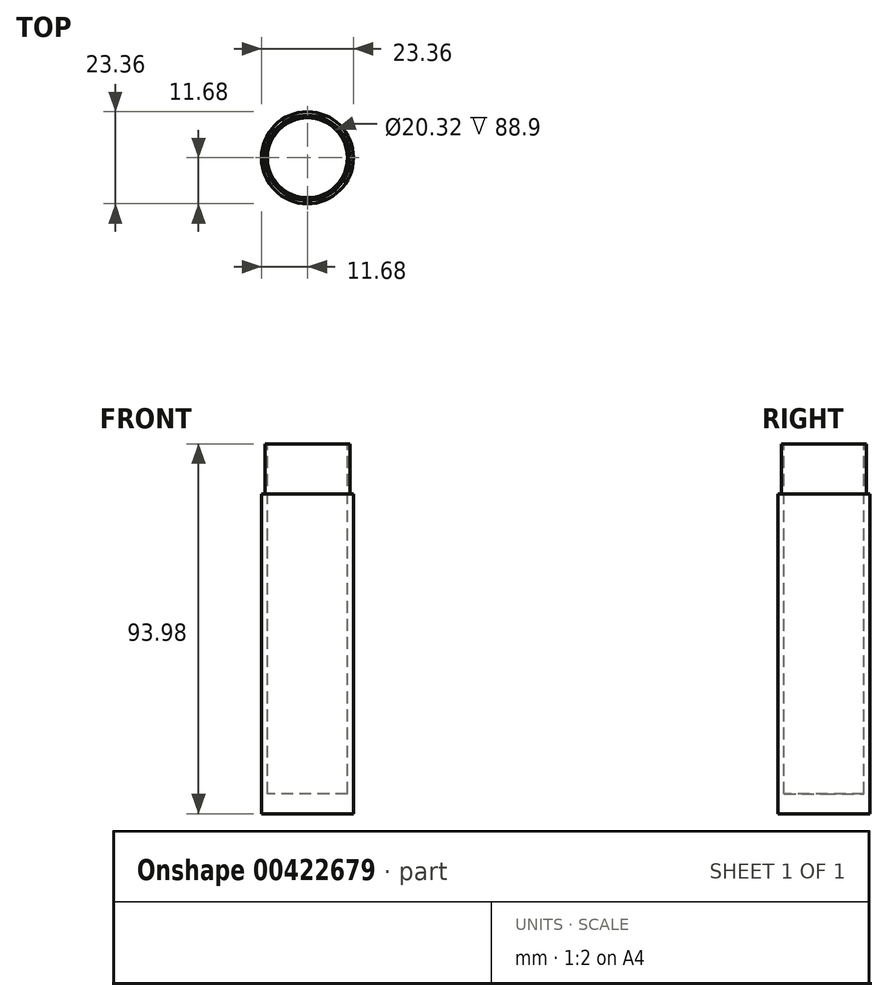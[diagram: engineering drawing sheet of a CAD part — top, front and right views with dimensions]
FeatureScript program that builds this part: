
annotation { "Feature Type Name" : "Feature", "Feature Type Description" : "" }
export const myFeature = defineFeature(function(context is Context, id is Id, definition is map)
    precondition{}
    {
        {
            var Q0;
            Q0=qCreatedBy(makeId("Top.planeOp"),FACE);
            var sketch = newSketch(context, id + "F0", { "sketchPlane" : qUnion([Q0])});
            skCircle(sketch, "E0", {"center": v(0, 0) * mm, "radius": 11.68 * mm});
            skSolve(sketch);
        }
        {
            var Q0;
            Q0=makeQuery(id+"F0.imprint","IMPRINT",FACE,{"disambiguationData":[TD([[makeQuery(id+"F0.imprint","IMPRINT",EDGE,{"derivedFrom":sQuery(id+"F0.wireOp",EDGE,"E0")}),1.0]])]});
            extrude(context, id + "F1", {"entities" : qUnion([Q0]), "depth" : 78.74 * mm});
        }
        {
            var Q0;
            Q0=makeQuery(id+"F1.opExtrude","CAP_FACE",FACE,{"disambiguationData":[OSD([sQuery(id+"F0.wireOp",EDGE,"E0")])],"isStart":false});
            var sketch = newSketch(context, id + "F2", { "sketchPlane" : qUnion([Q0])});
            skCircle(sketch, "E1", {"center": v(0, 0) * mm, "radius": 10.16 * mm});
            skSolve(sketch);
        }
        {
            var Q0;
            Q0=makeQuery(id+"F2.imprint","IMPRINT",FACE,{"disambiguationData":[TD([[makeQuery(id+"F2.imprint","IMPRINT",EDGE,{"derivedFrom":sQuery(id+"F2.wireOp",EDGE,"E1")}),1.0]])]});
            extrude(context, id + "F3", {"entities" : qUnion([Q0]), "operationType" : NewBodyOperationType.REMOVE, "oppositeDirection" : true, "depth" : 76.2 * mm});
        }
        {
            var Q0;
            Q0=makeQuery(id+"F1.opExtrude","CAP_FACE",FACE,{"disambiguationData":[OSD([sQuery(id+"F0.wireOp",EDGE,"E0")])],"isStart":true});
            extrude(context, id + "F4", {"entities" : qUnion([Q0]), "operationType" : NewBodyOperationType.ADD, "depth" : 2.54 * mm});
        }
        {
            var Q0;
            Q0=makeQuery(id+"F4.opExtrude","CAP_FACE",FACE,{"disambiguationData":[OSD([sQuery(id+"F0.wireOp",EDGE,"E0")])],"isStart":false});
            extrude(context, id + "F5", {"entities" : qUnion([Q0]), "operationType" : NewBodyOperationType.ADD, "depth" : 7.62 * mm});
        }
        {
            var Q0;
            Q0=makeQuery(id+"F2.imprint","IMPRINT",FACE,{"disambiguationData":[TD([[makeQuery(id+"F2.imprint","IMPRINT",EDGE,{"derivedFrom":sQuery(id+"F2.wireOp",EDGE,"E1")}),-1.0]])]});
            var sketch = newSketch(context, id + "F6", { "sketchPlane" : qUnion([Q0])});
            skCircle(sketch, "E2", {"center": v(0, 0) * mm, "radius": 10.8 * mm});
            skSolve(sketch);
        }
        {
            var Q0;
            Q0=makeQuery(id+"F5.opExtrude","CAP_FACE",FACE,{"disambiguationData":[OSD([sQuery(id+"F0.wireOp",EDGE,"E0")])],"isStart":false});
            extrude(context, id + "F7", {"entities" : qUnion([Q0]), "operationType" : NewBodyOperationType.REMOVE, "oppositeDirection" : true, "depth" : 7.62 * mm});
        }
        {
            var Q0;
            Q0=makeQuery(id+"F2.imprint","IMPRINT",FACE,{"disambiguationData":[TD([[makeQuery(id+"F2.imprint","IMPRINT",EDGE,{"derivedFrom":sQuery(id+"F2.wireOp",EDGE,"E1")}),-1.0]])]});
            var sketch = newSketch(context, id + "F8", { "sketchPlane" : qUnion([Q0])});
            skCircle(sketch, "E3", {"center": v(0, 0) * mm, "radius": 10.74 * mm});
            skSolve(sketch);
        }
        {
            var Q0;
            Q0=makeQuery(id+"F6.imprint","IMPRINT",FACE,{"disambiguationData":[TD([[makeQuery(id+"F6.imprint","IMPRINT",EDGE,{"derivedFrom":sQuery(id+"F6.wireOp",EDGE,"E2")}),1.0]])]});
            var Q1;
            Q1=sQuery(id+"F8.wireOp",EDGE,"E3");
            var Q2;
            Q2=sQuery(id+"F2.wireOp",EDGE,"E1");
            extrude(context, id + "F9", {"entities" : qUnion([Q0]), "operationType" : NewBodyOperationType.ADD, "surfaceEntities" : qUnion([Q1, Q2]), "depth" : 12.7 * mm});
        }
    });
